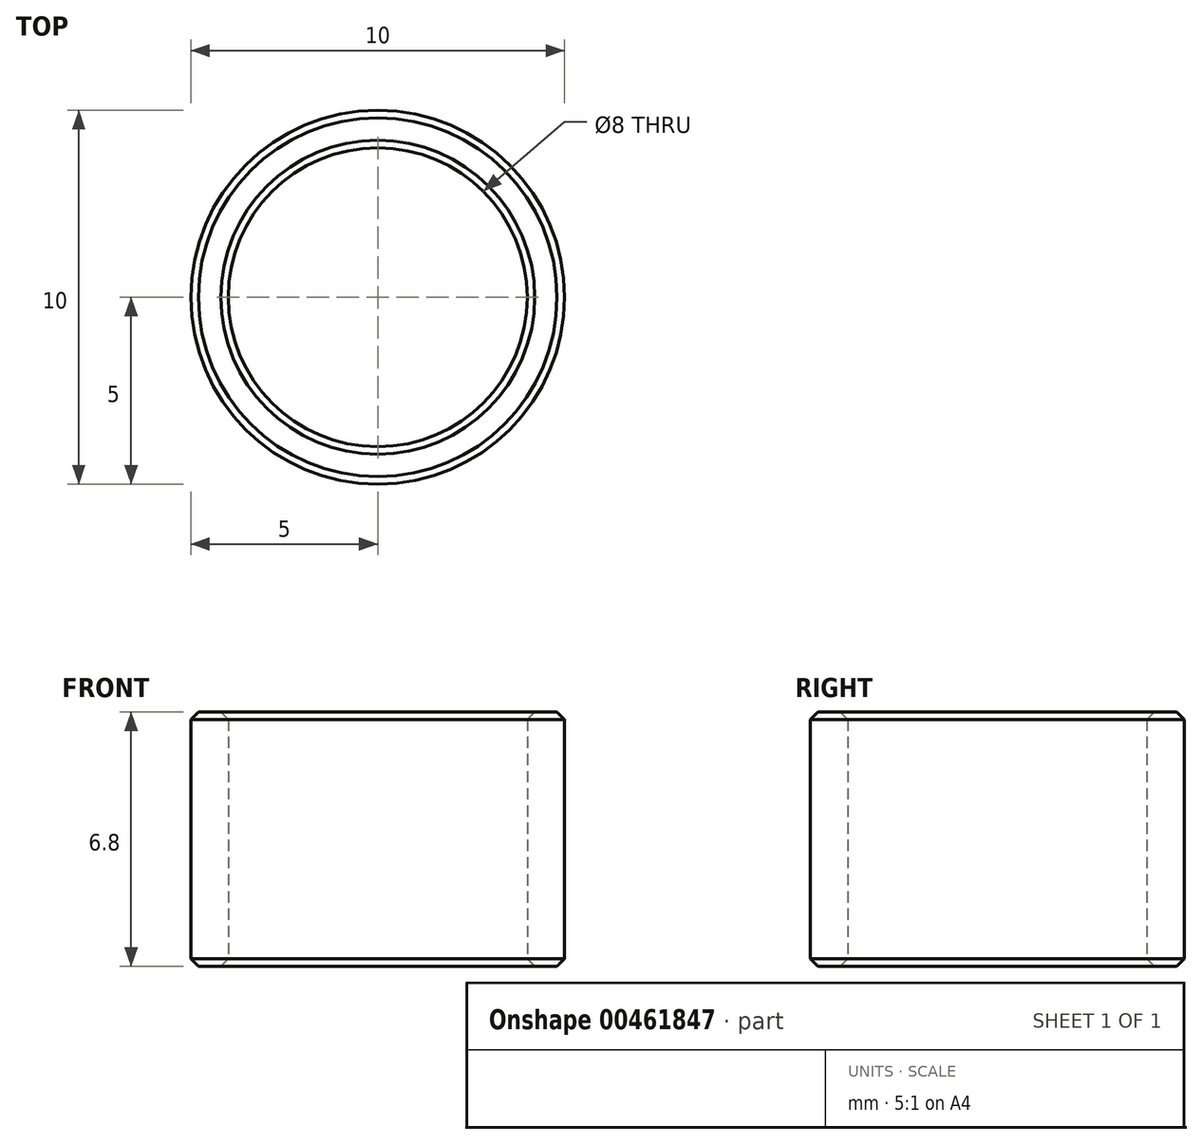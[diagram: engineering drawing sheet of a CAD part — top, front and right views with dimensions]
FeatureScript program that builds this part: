
annotation { "Feature Type Name" : "Feature", "Feature Type Description" : "" }
export const myFeature = defineFeature(function(context is Context, id is Id, definition is map)
    precondition{}
    {
        {
            var Q0;
            Q0=qCreatedBy(makeId("Top.planeOp"),FACE);
            var sketch = newSketch(context, id + "F0", { "sketchPlane" : qUnion([Q0])});
            skCircle(sketch, "E0", {"center": v(0, 0) * mm, "radius": 4 * mm});
            skCircle(sketch, "E1", {"center": v(0, 0) * mm, "radius": 5 * mm});
            skSolve(sketch);
        }
        {
            var Q0;
            Q0 = qSketchRegion(id + "F0", true);
            extrude(context, id + "F1", {"entities" : qUnion([Q0]), "depth" : 6.8 * mm});
        }
        {
            var Q0;
            Q0=makeQuery(id+"F1.opExtrude","CAP_EDGE",EDGE,{"disambiguationData":[OSD([sQuery(id+"F0.wireOp",EDGE,"E0")])],"isStart":false});
            chamfer(context, id + "F2", {"entities" : qUnion([Q0]), "width" : 0.2 * mm, "tangentPropagation" : true});
        }
        {
            var Q0;
            Q0=makeQuery(id+"F1.opExtrude","CAP_EDGE",EDGE,{"disambiguationData":[OSD([sQuery(id+"F0.wireOp",EDGE,"E1")])],"isStart":false});
            chamfer(context, id + "F3", {"entities" : qUnion([Q0]), "width" : 0.2 * mm, "tangentPropagation" : true});
        }
        {
            var Q0;
            Q0=makeQuery(id+"F1.opExtrude","CAP_EDGE",EDGE,{"disambiguationData":[OSD([sQuery(id+"F0.wireOp",EDGE,"E1")])],"isStart":true});
            var Q1;
            Q1=makeQuery(id+"F1.opExtrude","CAP_EDGE",EDGE,{"disambiguationData":[OSD([sQuery(id+"F0.wireOp",EDGE,"E0")])],"isStart":true});
            chamfer(context, id + "F4", {"entities" : qUnion([Q0, Q1]), "width" : 0.2 * mm, "tangentPropagation" : true});
        }
    });
